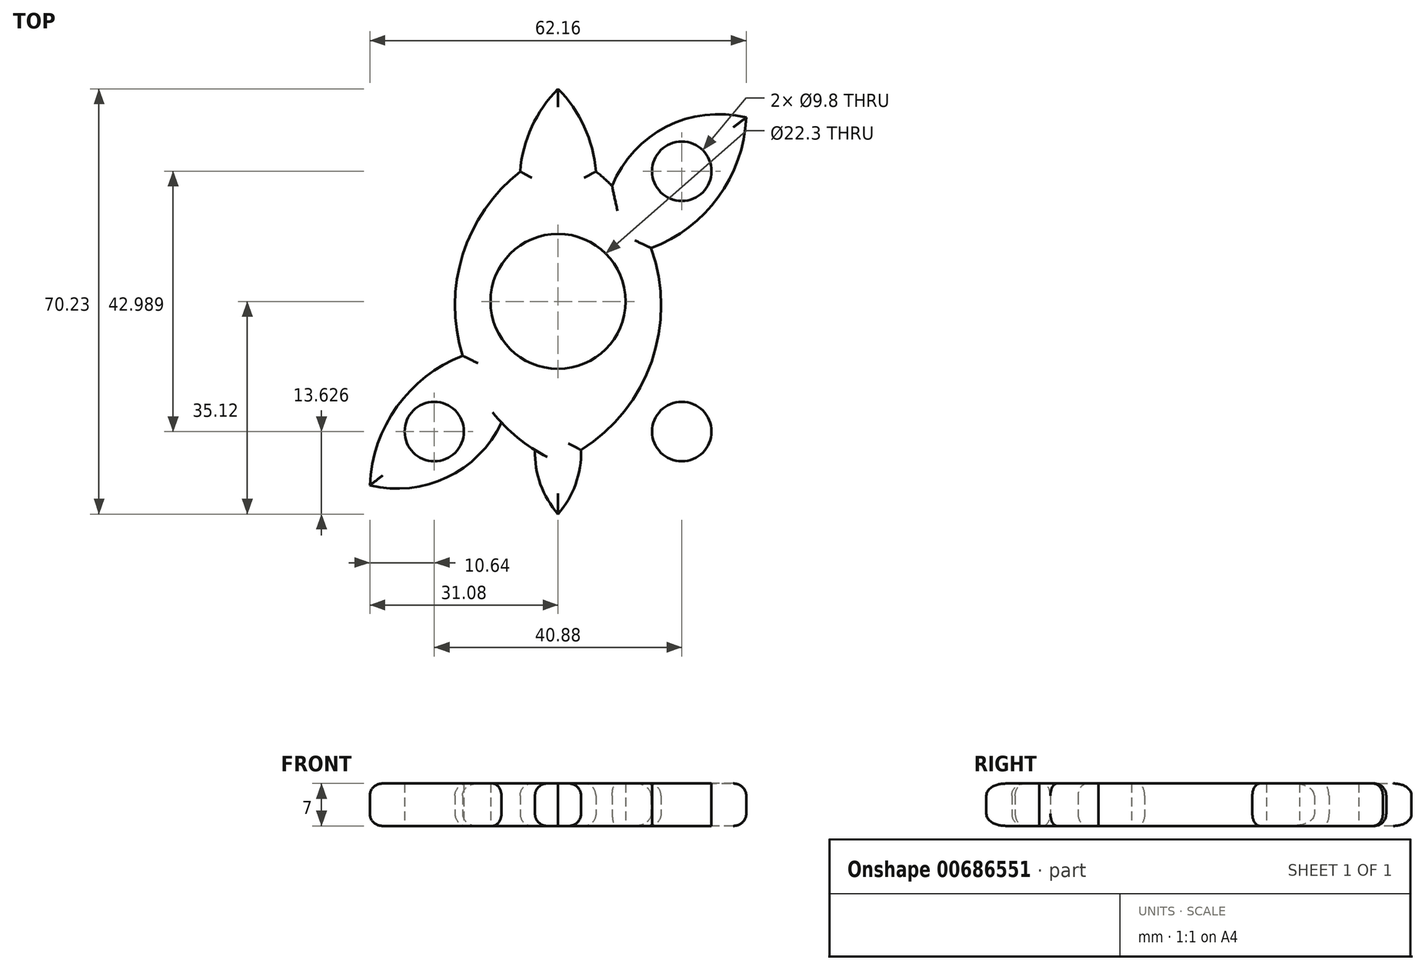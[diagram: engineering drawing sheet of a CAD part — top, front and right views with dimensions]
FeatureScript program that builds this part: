
annotation { "Feature Type Name" : "Feature", "Feature Type Description" : "" }
export const myFeature = defineFeature(function(context is Context, id is Id, definition is map)
    precondition{}
    {
        {
            var Q0;
            Q0=qCreatedBy(makeId("Top.planeOp"),FACE);
            var sketch = newSketch(context, id + "F0", { "sketchPlane" : qUnion([Q0])});
            skArc(sketch, "E0", {"start": v(0, -26.55) * mm, "mid": v(17.03, -0.69) * mm, "end": v(0, 25.18) * mm});
            skCircle(sketch, "E1", {"center": v(0, 0) * mm, "radius": 11.15 * mm});
            skArc(sketch, "E2.MirrorCS", {"start": v(0, -26.55) * mm, "mid": v(-17.03, -0.69) * mm, "end": v(0, 25.18) * mm});
            skArc(sketch, "E3", {"start": v(0, -35.12) * mm, "mid": v(2.9, -30.2) * mm, "end": v(3.8, -24.56) * mm});
            skArc(sketch, "E4", {"start": v(31.08, 30.36) * mm, "mid": v(17.9, 28.85) * mm, "end": v(8.94, 19.06) * mm});
            skArc(sketch, "E5", {"start": v(15.37, 8.81) * mm, "mid": v(26.48, 17.22) * mm, "end": v(31.08, 30.36) * mm});
            skCircle(sketch, "E6", {"center": v(20.44, 21.5) * mm, "radius": 4.9 * mm});
            skArc(sketch, "E7", {"start": v(6.26, 21.46) * mm, "mid": v(4.34, 28.84) * mm, "end": v(0, 35.1) * mm});
            skArc(sketch, "E8.MirrorCS", {"start": v(15.37, -8.81) * mm, "mid": v(26.48, -17.22) * mm, "end": v(31.08, -30.36) * mm});
            skArc(sketch, "E9.MirrorCS", {"start": v(31.08, -30.36) * mm, "mid": v(17.9, -28.85) * mm, "end": v(8.94, -19.06) * mm});
            skCircle(sketch, "E10.MirrorC", {"center": v(20.44, -21.5) * mm, "radius": 4.9 * mm});
            skArc(sketch, "E11.MirrorCS", {"start": v(-31.08, 30.36) * mm, "mid": v(-17.9, 28.85) * mm, "end": v(-8.94, 19.06) * mm});
            skCircle(sketch, "E12.MirrorC", {"center": v(-20.44, 21.5) * mm, "radius": 4.9 * mm});
            skArc(sketch, "E13.MirrorCS", {"start": v(-15.37, 8.81) * mm, "mid": v(-26.48, 17.22) * mm, "end": v(-31.08, 30.36) * mm});
            skArc(sketch, "E14.MirrorCS", {"start": v(-15.37, -8.81) * mm, "mid": v(-26.48, -17.22) * mm, "end": v(-31.08, -30.36) * mm});
            skCircle(sketch, "E15.MirrorC", {"center": v(-20.44, -21.5) * mm, "radius": 4.9 * mm});
            skArc(sketch, "E16.MirrorCS", {"start": v(-31.08, -30.36) * mm, "mid": v(-17.9, -28.85) * mm, "end": v(-8.94, -19.06) * mm});
            skArc(sketch, "E17.MirrorCS", {"start": v(-6.26, 21.46) * mm, "mid": v(-4.34, 28.84) * mm, "end": v(0, 35.1) * mm});
            skArc(sketch, "E18.MirrorCS", {"start": v(0, -35.12) * mm, "mid": v(-2.9, -30.2) * mm, "end": v(-3.8, -24.56) * mm});
            skSolve(sketch);
        }
        {
            var Q0;
            {var subQ3=sQuery(id+"F0.wireOp",EDGE,"E7");Q0=makeQuery(id+"F0.imprint","IMPRINT",FACE,{"disambiguationData":[TD([[makeQuery(id+"F0.imprint","IMPRINT",EDGE,{"derivedFrom":subQ3}),1.0]])]});}
            var Q1;
            Q1=makeQuery(id+"F0.imprint","IMPRINT",FACE,{"disambiguationData":[TD([[makeQuery(id+"F0.imprint","IMPRINT",EDGE,{"derivedFrom":sQuery(id+"F0.wireOp",EDGE,"E1")}),-1.0]])]});
            var Q2;
            {var subQ0=sQuery(id+"F0.wireOp",EDGE,"E11.MirrorCS");Q2=makeQuery(id+"F0.imprint","IMPRINT",FACE,{"disambiguationData":[TD([[makeQuery(id+"F0.imprint","IMPRINT",EDGE,{"derivedFrom":subQ0}),-1.0]])]});}
            var Q3;
            {var subQ0=sQuery(id+"F0.wireOp",EDGE,"E4");Q3=makeQuery(id+"F0.imprint","IMPRINT",FACE,{"disambiguationData":[TD([[makeQuery(id+"F0.imprint","IMPRINT",EDGE,{"derivedFrom":subQ0}),1.0]])]});}
            var Q4;
            Q4=makeQuery(id+"F0.imprint","IMPRINT",FACE,{"disambiguationData":[TD([[makeQuery(id+"F0.imprint","IMPRINT",EDGE,{"derivedFrom":sQuery(id+"F0.wireOp",EDGE,"E10.MirrorC")}),1.0]])]});
            var Q5;
            {var subQ3=sQuery(id+"F0.wireOp",EDGE,"E3");Q5=makeQuery(id+"F0.imprint","IMPRINT",FACE,{"disambiguationData":[TD([[makeQuery(id+"F0.imprint","IMPRINT",EDGE,{"derivedFrom":subQ3}),1.0]])]});}
            var Q6;
            Q6=makeQuery(id+"F0.imprint","IMPRINT",FACE,{"disambiguationData":[TD([[makeQuery(id+"F0.imprint","IMPRINT",EDGE,{"derivedFrom":sQuery(id+"F0.wireOp",EDGE,"E15.MirrorC")}),-1.0]])]});
            extrude(context, id + "F1", {"entities" : qUnion([Q0, Q1, Q2, Q3, Q4, Q5, Q6]), "depth" : 7 * mm, "offsetDistance" : 25 * mm});
        }
        {
            var Q0;
            {var subQ0=sQuery(id+"F0.wireOp",EDGE,"E2.MirrorCS");Q0=makeQuery(id+"F1.opExtrude","CAP_EDGE",EDGE,{"disambiguationData":[OSD([subQ0]),TDD([makeQuery(id+"F0.imprint","IMPRINT",EDGE,{"disambiguationData":[TD([[makeQuery(id+"F0.imprint","INTERSECT",VERTEX,{"derivedFrom":[subQ0,sQuery(id+"F0.wireOp",EDGE,"E18.MirrorCS")]}),-1.0]])],"derivedFrom":subQ0})])],"isStart":false});}
            var Q1;
            Q1=makeQuery(id+"F1.opExtrude","CAP_EDGE",EDGE,{"disambiguationData":[OSD([sQuery(id+"F0.wireOp",EDGE,"E18.MirrorCS")])],"isStart":false});
            var Q2;
            {var subQ0=sQuery(id+"F0.wireOp",EDGE,"E0");Q2=makeQuery(id+"F1.opExtrude","CAP_EDGE",EDGE,{"disambiguationData":[OSD([subQ0]),TDD([makeQuery(id+"F0.imprint","IMPRINT",EDGE,{"disambiguationData":[TD([[makeQuery(id+"F0.imprint","INTERSECT",VERTEX,{"derivedFrom":[subQ0,sQuery(id+"F0.wireOp",EDGE,"E3")]}),-1.0]])],"derivedFrom":subQ0})])],"isStart":false});}
            var Q3;
            Q3=makeQuery(id+"F1.opExtrude","CAP_EDGE",EDGE,{"disambiguationData":[OSD([sQuery(id+"F0.wireOp",EDGE,"E3")])],"isStart":false});
            var Q4;
            Q4=makeQuery(id+"F1.opExtrude","CAP_EDGE",EDGE,{"disambiguationData":[OSD([sQuery(id+"F0.wireOp",EDGE,"E16.MirrorCS")])],"isStart":false});
            var Q5;
            Q5=makeQuery(id+"F1.opExtrude","CAP_EDGE",EDGE,{"disambiguationData":[OSD([sQuery(id+"F0.wireOp",EDGE,"E14.MirrorCS")])],"isStart":false});
            var Q6;
            {var subQ0=sQuery(id+"F0.wireOp",EDGE,"E2.MirrorCS");Q6=makeQuery(id+"F1.opExtrude","CAP_EDGE",EDGE,{"disambiguationData":[OSD([subQ0]),TDD([makeQuery(id+"F0.imprint","IMPRINT",EDGE,{"disambiguationData":[TD([[makeQuery(id+"F0.imprint","INTERSECT",VERTEX,{"derivedFrom":[subQ0,sQuery(id+"F0.wireOp",EDGE,"E13.MirrorCS")]}),1.0]])],"derivedFrom":subQ0})])],"isStart":false});}
            var Q7;
            Q7=makeQuery(id+"F1.opExtrude","CAP_EDGE",EDGE,{"disambiguationData":[OSD([sQuery(id+"F0.wireOp",EDGE,"E9.MirrorCS")])],"isStart":false});
            var Q8;
            Q8=makeQuery(id+"F1.opExtrude","CAP_EDGE",EDGE,{"disambiguationData":[OSD([sQuery(id+"F0.wireOp",EDGE,"E8.MirrorCS")])],"isStart":false});
            var Q9;
            Q9=makeQuery(id+"F1.opExtrude","CAP_EDGE",EDGE,{"disambiguationData":[OSD([sQuery(id+"F0.wireOp",EDGE,"E5")])],"isStart":false});
            var Q10;
            Q10=makeQuery(id+"F1.opExtrude","CAP_EDGE",EDGE,{"disambiguationData":[OSD([sQuery(id+"F0.wireOp",EDGE,"E4")])],"isStart":false});
            var Q11;
            {var subQ0=sQuery(id+"F0.wireOp",EDGE,"E0");Q11=makeQuery(id+"F1.opExtrude","CAP_EDGE",EDGE,{"disambiguationData":[OSD([subQ0]),TDD([makeQuery(id+"F0.imprint","IMPRINT",EDGE,{"disambiguationData":[TD([[makeQuery(id+"F0.imprint","INTERSECT",VERTEX,{"derivedFrom":[subQ0,sQuery(id+"F0.wireOp",EDGE,"E4")]}),-1.0]])],"derivedFrom":subQ0})])],"isStart":false});}
            var Q12;
            Q12=makeQuery(id+"F1.opExtrude","CAP_EDGE",EDGE,{"disambiguationData":[OSD([sQuery(id+"F0.wireOp",EDGE,"E7")])],"isStart":false});
            var Q13;
            Q13=makeQuery(id+"F1.opExtrude","CAP_EDGE",EDGE,{"disambiguationData":[OSD([sQuery(id+"F0.wireOp",EDGE,"E17.MirrorCS")])],"isStart":false});
            var Q14;
            {var subQ0=sQuery(id+"F0.wireOp",EDGE,"E2.MirrorCS");Q14=makeQuery(id+"F1.opExtrude","CAP_EDGE",EDGE,{"disambiguationData":[OSD([subQ0]),TDD([makeQuery(id+"F0.imprint","IMPRINT",EDGE,{"disambiguationData":[TD([[makeQuery(id+"F0.imprint","INTERSECT",VERTEX,{"derivedFrom":[subQ0,sQuery(id+"F0.wireOp",EDGE,"E11.MirrorCS")]}),-1.0]])],"derivedFrom":subQ0})])],"isStart":false});}
            var Q15;
            Q15=makeQuery(id+"F1.opExtrude","CAP_EDGE",EDGE,{"disambiguationData":[OSD([sQuery(id+"F0.wireOp",EDGE,"E11.MirrorCS")])],"isStart":false});
            var Q16;
            Q16=makeQuery(id+"F1.opExtrude","CAP_EDGE",EDGE,{"disambiguationData":[OSD([sQuery(id+"F0.wireOp",EDGE,"E13.MirrorCS")])],"isStart":false});
            var Q17;
            {var subQ0=sQuery(id+"F0.wireOp",EDGE,"E0");Q17=makeQuery(id+"F1.opExtrude","CAP_EDGE",EDGE,{"disambiguationData":[OSD([subQ0]),TDD([makeQuery(id+"F0.imprint","IMPRINT",EDGE,{"disambiguationData":[TD([[makeQuery(id+"F0.imprint","INTERSECT",VERTEX,{"derivedFrom":[subQ0,sQuery(id+"F0.wireOp",EDGE,"E4")]}),-1.0]])],"derivedFrom":subQ0})])],"isStart":true});}
            var Q18;
            Q18=makeQuery(id+"F1.opExtrude","CAP_EDGE",EDGE,{"disambiguationData":[OSD([sQuery(id+"F0.wireOp",EDGE,"E7")])],"isStart":true});
            var Q19;
            Q19=makeQuery(id+"F1.opExtrude","CAP_EDGE",EDGE,{"disambiguationData":[OSD([sQuery(id+"F0.wireOp",EDGE,"E4")])],"isStart":true});
            var Q20;
            Q20=makeQuery(id+"F1.opExtrude","CAP_EDGE",EDGE,{"disambiguationData":[OSD([sQuery(id+"F0.wireOp",EDGE,"E5")])],"isStart":true});
            var Q21;
            {var subQ0=sQuery(id+"F0.wireOp",EDGE,"E0");Q21=makeQuery(id+"F1.opExtrude","CAP_EDGE",EDGE,{"disambiguationData":[OSD([subQ0]),TDD([makeQuery(id+"F0.imprint","IMPRINT",EDGE,{"disambiguationData":[TD([[makeQuery(id+"F0.imprint","INTERSECT",VERTEX,{"derivedFrom":[subQ0,sQuery(id+"F0.wireOp",EDGE,"E5")]}),1.0]])],"derivedFrom":subQ0})])],"isStart":true});}
            var Q22;
            Q22=makeQuery(id+"F1.opExtrude","CAP_EDGE",EDGE,{"disambiguationData":[OSD([sQuery(id+"F0.wireOp",EDGE,"E8.MirrorCS")])],"isStart":true});
            var Q23;
            Q23=makeQuery(id+"F1.opExtrude","CAP_EDGE",EDGE,{"disambiguationData":[OSD([sQuery(id+"F0.wireOp",EDGE,"E9.MirrorCS")])],"isStart":true});
            var Q24;
            {var subQ0=sQuery(id+"F0.wireOp",EDGE,"E0");Q24=makeQuery(id+"F1.opExtrude","CAP_EDGE",EDGE,{"disambiguationData":[OSD([subQ0]),TDD([makeQuery(id+"F0.imprint","IMPRINT",EDGE,{"disambiguationData":[TD([[makeQuery(id+"F0.imprint","INTERSECT",VERTEX,{"derivedFrom":[subQ0,sQuery(id+"F0.wireOp",EDGE,"E3")]}),-1.0]])],"derivedFrom":subQ0})])],"isStart":true});}
            var Q25;
            Q25=makeQuery(id+"F1.opExtrude","CAP_EDGE",EDGE,{"disambiguationData":[OSD([sQuery(id+"F0.wireOp",EDGE,"E3")])],"isStart":true});
            var Q26;
            Q26=makeQuery(id+"F1.opExtrude","CAP_EDGE",EDGE,{"disambiguationData":[OSD([sQuery(id+"F0.wireOp",EDGE,"E18.MirrorCS")])],"isStart":true});
            var Q27;
            {var subQ0=sQuery(id+"F0.wireOp",EDGE,"E2.MirrorCS");Q27=makeQuery(id+"F1.opExtrude","CAP_EDGE",EDGE,{"disambiguationData":[OSD([subQ0]),TDD([makeQuery(id+"F0.imprint","IMPRINT",EDGE,{"disambiguationData":[TD([[makeQuery(id+"F0.imprint","INTERSECT",VERTEX,{"derivedFrom":[subQ0,sQuery(id+"F0.wireOp",EDGE,"E18.MirrorCS")]}),-1.0]])],"derivedFrom":subQ0})])],"isStart":true});}
            var Q28;
            Q28=makeQuery(id+"F1.opExtrude","CAP_EDGE",EDGE,{"disambiguationData":[OSD([sQuery(id+"F0.wireOp",EDGE,"E16.MirrorCS")])],"isStart":true});
            var Q29;
            Q29=makeQuery(id+"F1.opExtrude","CAP_EDGE",EDGE,{"disambiguationData":[OSD([sQuery(id+"F0.wireOp",EDGE,"E14.MirrorCS")])],"isStart":true});
            var Q30;
            {var subQ0=sQuery(id+"F0.wireOp",EDGE,"E2.MirrorCS");Q30=makeQuery(id+"F1.opExtrude","CAP_EDGE",EDGE,{"disambiguationData":[OSD([subQ0]),TDD([makeQuery(id+"F0.imprint","IMPRINT",EDGE,{"disambiguationData":[TD([[makeQuery(id+"F0.imprint","INTERSECT",VERTEX,{"derivedFrom":[subQ0,sQuery(id+"F0.wireOp",EDGE,"E13.MirrorCS")]}),1.0]])],"derivedFrom":subQ0})])],"isStart":true});}
            var Q31;
            Q31=makeQuery(id+"F1.opExtrude","CAP_EDGE",EDGE,{"disambiguationData":[OSD([sQuery(id+"F0.wireOp",EDGE,"E13.MirrorCS")])],"isStart":true});
            var Q32;
            Q32=makeQuery(id+"F1.opExtrude","CAP_EDGE",EDGE,{"disambiguationData":[OSD([sQuery(id+"F0.wireOp",EDGE,"E11.MirrorCS")])],"isStart":true});
            var Q33;
            {var subQ0=sQuery(id+"F0.wireOp",EDGE,"E2.MirrorCS");Q33=makeQuery(id+"F1.opExtrude","CAP_EDGE",EDGE,{"disambiguationData":[OSD([subQ0]),TDD([makeQuery(id+"F0.imprint","IMPRINT",EDGE,{"disambiguationData":[TD([[makeQuery(id+"F0.imprint","INTERSECT",VERTEX,{"derivedFrom":[subQ0,sQuery(id+"F0.wireOp",EDGE,"E11.MirrorCS")]}),-1.0]])],"derivedFrom":subQ0})])],"isStart":true});}
            var Q34;
            Q34=makeQuery(id+"F1.opExtrude","CAP_EDGE",EDGE,{"disambiguationData":[OSD([sQuery(id+"F0.wireOp",EDGE,"E17.MirrorCS")])],"isStart":true});
            var Q35;
            {var subQ0=sQuery(id+"F0.wireOp",EDGE,"E0");Q35=makeQuery(id+"F1.opExtrude","CAP_EDGE",EDGE,{"disambiguationData":[OSD([subQ0]),TDD([makeQuery(id+"F0.imprint","IMPRINT",EDGE,{"disambiguationData":[TD([[makeQuery(id+"F0.imprint","INTERSECT",VERTEX,{"derivedFrom":[subQ0,sQuery(id+"F0.wireOp",EDGE,"E5")]}),1.0]])],"derivedFrom":subQ0})])],"isStart":false});}
            fillet(context, id + "F2", {"entities" : qUnion([Q0, Q1, Q2, Q3, Q4, Q5, Q6, Q7, Q8, Q9, Q10, Q11, Q12, Q13, Q14, Q15, Q16, Q17, Q18, Q19, Q20, Q21, Q22, Q23, Q24, Q25, Q26, Q27, Q28, Q29, Q30, Q31, Q32, Q33, Q34, Q35]), "radius" : 2 * mm, "tangentPropagation" : true, "allowEdgeOverflow" : false});
        }
    });
